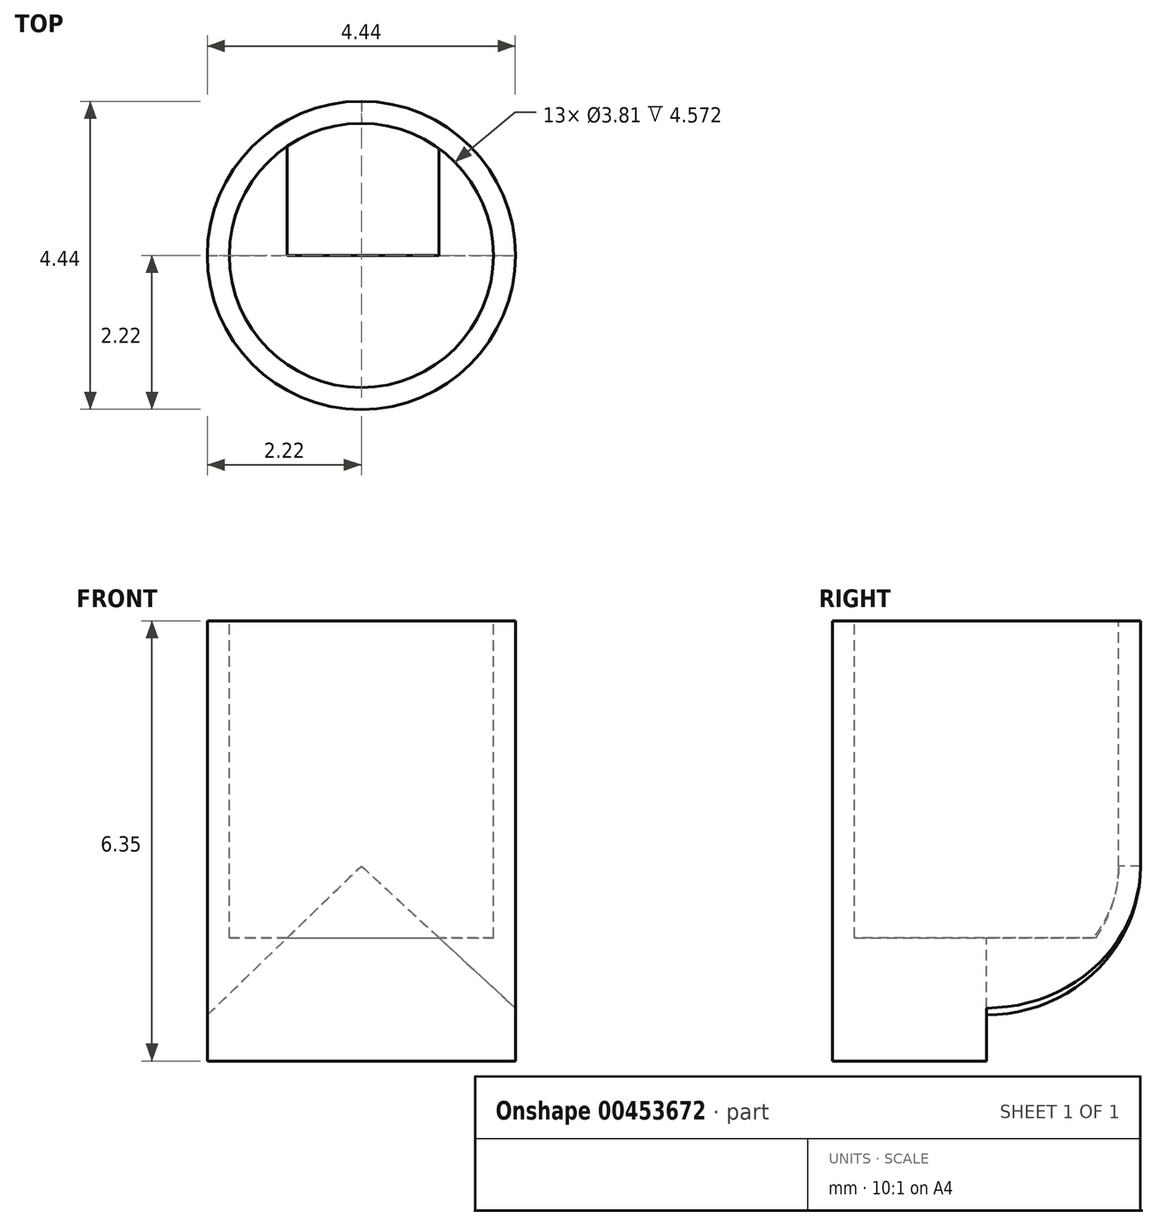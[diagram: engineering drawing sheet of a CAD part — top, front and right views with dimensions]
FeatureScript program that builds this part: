
annotation { "Feature Type Name" : "Feature", "Feature Type Description" : "" }
export const myFeature = defineFeature(function(context is Context, id is Id, definition is map)
    precondition{}
    {
        {
            var Q0;
            Q0=qCreatedBy(makeId("Top.planeOp"),FACE);
            var sketch = newSketch(context, id + "F0", { "sketchPlane" : qUnion([Q0])});
            skCircle(sketch, "E0", {"center": v(0, 0) * mm, "radius": 2.22 * mm});
            skSolve(sketch);
        }
        {
            var Q0;
            Q0=makeQuery(id+"F0.imprint","IMPRINT",FACE,{"disambiguationData":[TD([[makeQuery(id+"F0.imprint","IMPRINT",EDGE,{"derivedFrom":sQuery(id+"F0.wireOp",EDGE,"E0")}),1.0]])]});
            extrude(context, id + "F1", {"entities" : qUnion([Q0]), "depth" : 6.35 * mm});
        }
        {
            var Q0;
            Q0=makeQuery(id+"F1.opExtrude","CAP_FACE",FACE,{"disambiguationData":[OSD([sQuery(id+"F0.wireOp",EDGE,"E0")])],"isStart":false});
            var sketch = newSketch(context, id + "F2", { "sketchPlane" : qUnion([Q0])});
            skCircle(sketch, "E1", {"center": v(0, 0) * mm, "radius": 1.9 * mm});
            skSolve(sketch);
        }
        {
            var Q0;
            Q0 = qSketchRegion(id + "F2", true);
            extrude(context, id + "F3", {"entities" : qUnion([Q0]), "operationType" : NewBodyOperationType.REMOVE, "oppositeDirection" : true, "depth" : 4.57 * mm});
        }
        {
            var Q0;
            Q0=qCreatedBy(makeId("Front.planeOp"),FACE);
            var sketch = newSketch(context, id + "F4", { "sketchPlane" : qUnion([Q0])});
            skLineSegment(sketch, "E2", {"start": v(-2.9, 0) * mm, "end": v(0, 2.81) * mm});
            skLineSegment(sketch, "E3", {"start": v(0, 2.81) * mm, "end": v(3.05, 0) * mm});
            skLineSegment(sketch, "E4", {"start": v(-2.9, 0) * mm, "end": v(3.05, 0) * mm});
            skSolve(sketch);
        }
        {
            var Q0;
            Q0 = qSketchRegion(id + "F4", true);
            extrude(context, id + "F5", {"entities" : qUnion([Q0]), "operationType" : NewBodyOperationType.REMOVE, "endBound" : BoundingType.THROUGH_ALL, "oppositeDirection" : true, "depth" : 25.4 * mm});
        }
    });
